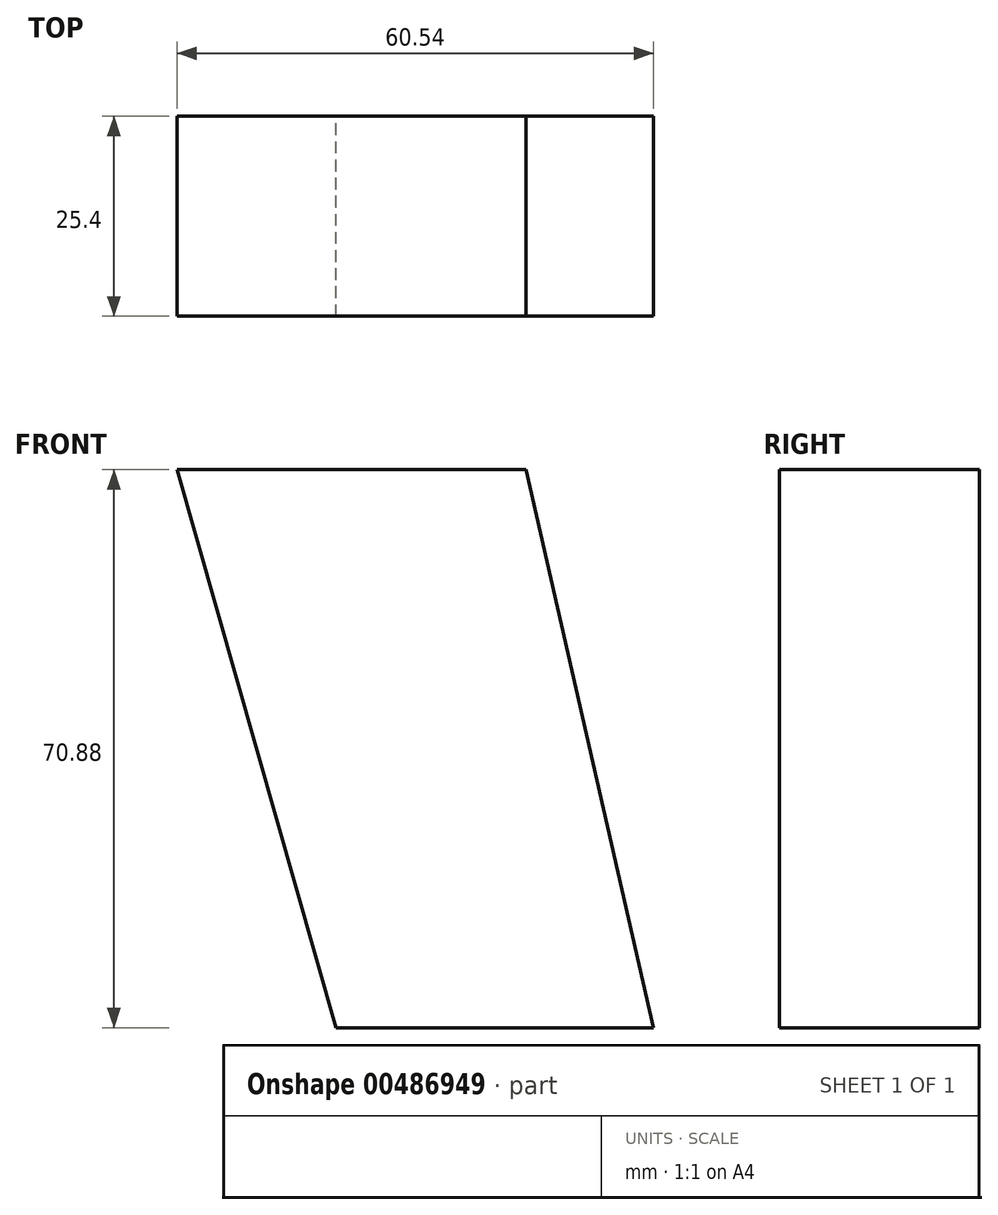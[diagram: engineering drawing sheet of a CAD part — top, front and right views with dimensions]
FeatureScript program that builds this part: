
annotation { "Feature Type Name" : "Feature", "Feature Type Description" : "" }
export const myFeature = defineFeature(function(context is Context, id is Id, definition is map)
    precondition{}
    {
        {
            var Q0;
            Q0=qCreatedBy(makeId("Front.planeOp"),FACE);
            var sketch = newSketch(context, id + "F0", { "sketchPlane" : qUnion([Q0])});
            skLineSegment(sketch, "E0", {"start": v(-96.59, 35.98) * mm, "end": v(-52.27, 35.98) * mm});
            skLineSegment(sketch, "E1", {"start": v(-52.27, 35.98) * mm, "end": v(-36.05, -34.9) * mm});
            skLineSegment(sketch, "E2", {"start": v(-36.05, -34.9) * mm, "end": v(-76.34, -34.9) * mm});
            skLineSegment(sketch, "E3", {"start": v(-76.34, -34.9) * mm, "end": v(-96.59, 35.98) * mm});
            skSolve(sketch);
        }
        {
            var Q0;
            Q0 = qSketchRegion(id + "F0", true);
            extrude(context, id + "F1", {"entities" : qUnion([Q0]), "depth" : 25.4 * mm});
        }
    });
